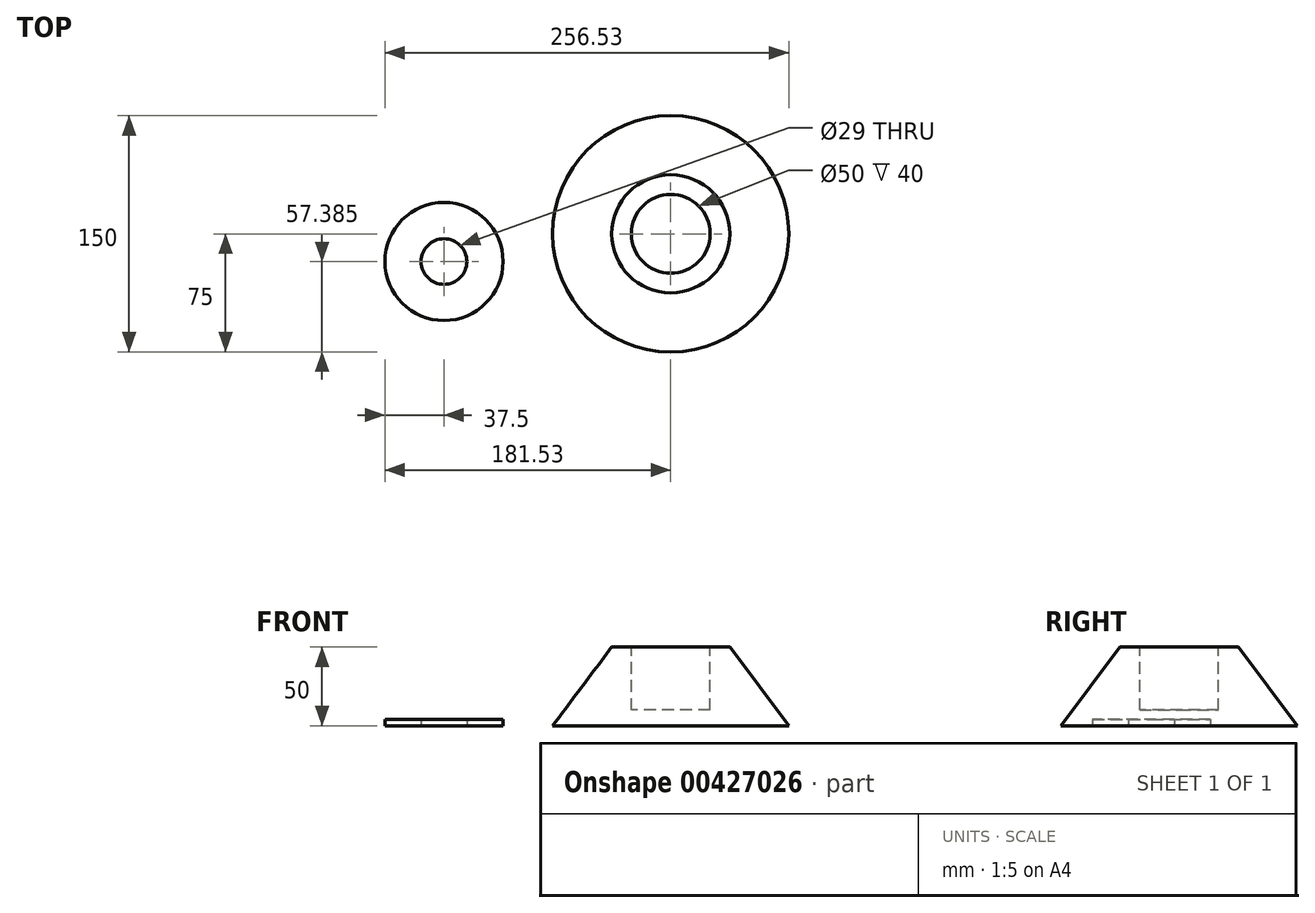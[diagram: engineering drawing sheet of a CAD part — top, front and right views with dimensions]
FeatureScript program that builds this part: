
annotation { "Feature Type Name" : "Feature", "Feature Type Description" : "" }
export const myFeature = defineFeature(function(context is Context, id is Id, definition is map)
    precondition{}
    {
        {
            var Q0;
            Q0=qCreatedBy(makeId("Front.planeOp"),FACE);
            var sketch = newSketch(context, id + "F0", { "sketchPlane" : qUnion([Q0])});
            skPoint(sketch, "E0.start.orphan", {"position": v(15, 0) * mm});
            skLineSegment(sketch, "E1", {"start": v(0, 0) * mm, "end": v(0, 50) * mm});
            skLineSegment(sketch, "E2", {"start": v(0, 50) * mm, "end": v(37.5, 50) * mm});
            skLineSegment(sketch, "E3", {"start": v(37.5, 50) * mm, "end": v(75, 0) * mm});
            skLineSegment(sketch, "E4", {"start": v(75, 0) * mm, "end": v(0, 0) * mm});
            skSolve(sketch);
        }
        {
            var Q0;
            Q0 = qSketchRegion(id + "F0", true);
            var Q1;
            Q1=sQuery(id+"F0.wireOp",EDGE,"E1");
            revolve(context, id + "F1", {"entities" : qUnion([Q0]), "axis" : qUnion([Q1]), "revolveType" : RevolveType.FULL});
        }
        {
            var Q0;
            Q0=makeQuery(id+"F1.opRevolve","SWEPT_FACE",FACE,{"disambiguationData":[OSD([sQuery(id+"F0.wireOp",EDGE,"E2")])]});
            var sketch = newSketch(context, id + "F2", { "sketchPlane" : qUnion([Q0])});
            skCircle(sketch, "E5", {"center": v(0, 0) * mm, "radius": 25 * mm});
            skSolve(sketch);
        }
        {
            var Q0;
            Q0=makeQuery(id+"F2.imprint","IMPRINT",FACE,{"disambiguationData":[TD([[makeQuery(id+"F2.imprint","IMPRINT",EDGE,{"derivedFrom":sQuery(id+"F2.wireOp",EDGE,"E5")}),1.0]])]});
            extrude(context, id + "F3", {"entities" : qUnion([Q0]), "operationType" : NewBodyOperationType.REMOVE, "oppositeDirection" : true, "depth" : 40 * mm});
        }
        {
            var Q0;
            Q0=qCreatedBy(makeId("Top.planeOp"),FACE);
            var sketch = newSketch(context, id + "F4", { "sketchPlane" : qUnion([Q0])});
            skCircle(sketch, "E6", {"center": v(-144.03, -17.62) * mm, "radius": 37.5 * mm});
            skCircle(sketch, "E7", {"center": v(-144.03, -17.62) * mm, "radius": 14.5 * mm});
            skSolve(sketch);
        }
        {
            var Q0;
            Q0=makeQuery(id+"F4.imprint","IMPRINT",FACE,{"disambiguationData":[TD([[makeQuery(id+"F4.imprint","IMPRINT",EDGE,{"derivedFrom":sQuery(id+"F4.wireOp",EDGE,"E6")}),1.0]])]});
            extrude(context, id + "F5", {"entities" : qUnion([Q0]), "depth" : 4 * mm, "offsetDistance" : 25 * mm});
        }
    });
